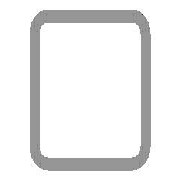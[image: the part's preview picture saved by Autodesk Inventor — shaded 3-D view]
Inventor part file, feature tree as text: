
AUTODESK INVENTOR PART (.ipt)
format: ipt  version: 2025 (Build 290162010, 162A)  size: 133,120 bytes
history: native  units: mm (DEFAULTED — no unit token found)
features: other x4, sketch x1, plane x1
ambient origin geometry x8: Origin, YZ Plane, XZ Plane, XY Plane, X Axis, Y Axis, Z Axis, Center Point
bodies: Solid1 (feature_tree), Body (feature_tree)
feature tree (6):
  parser-record x1  (decoder bookkeeping rows leaked as tree rows — omitted from the tree; the rows remain in map.json)
  other  "Driven Length"
  other  "Start Plane"
  other  "End Plane"
  sketch  "Sketch3"  dims[d3=5500.0mm d4=0.0mm d7=6.0mm d9=100.0mm d11=100.0mm d12=3.0mm d13=-0.0mm d14=5500.0mm d15=50.0mm d16=50.0mm d17=90.0deg d18=5500.0mm]
  plane  "Work Plane3"
